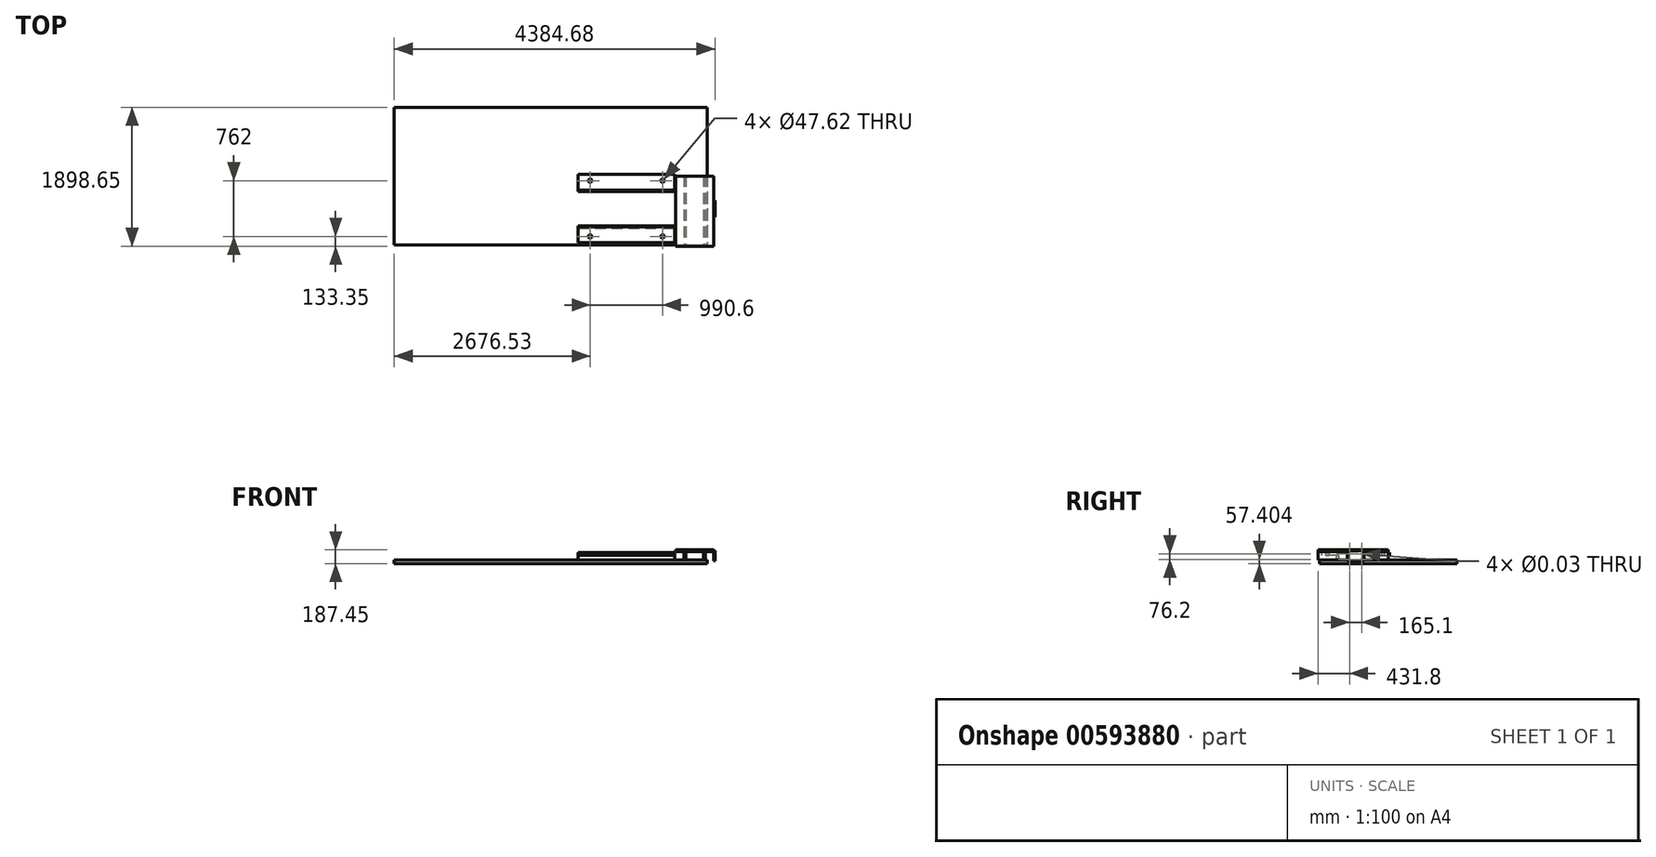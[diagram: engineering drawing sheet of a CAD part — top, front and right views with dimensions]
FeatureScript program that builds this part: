
annotation { "Feature Type Name" : "Feature", "Feature Type Description" : "" }
export const myFeature = defineFeature(function(context is Context, id is Id, definition is map)
    precondition{}
    {
        {
            var Q0;
            Q0=qCreatedBy(makeId("Top.planeOp"),FACE);
            var sketch = newSketch(context, id + "F0", { "sketchPlane" : qUnion([Q0])});
            skLineSegment(sketch, "E0.bottom", {"start": v(-2139.95, 939.8) * mm, "end": v(2139.95, 939.8) * mm});
            skLineSegment(sketch, "E0.top", {"start": v(-2139.95, -939.8) * mm, "end": v(2139.95, -939.8) * mm});
            skLineSegment(sketch, "E0.left", {"start": v(-2139.95, 939.8) * mm, "end": v(-2139.95, -939.8) * mm});
            skLineSegment(sketch, "E0.right", {"start": v(2139.95, 939.8) * mm, "end": v(2139.95, -939.8) * mm});
            skPoint(sketch, "E0.middle", {"position": v(0, 0) * mm});
            skSolve(sketch);
        }
        {
            var Q0;
            Q0 = qSketchRegion(id + "F0", true);
            extrude(context, id + "F1", {"entities" : qUnion([Q0]), "oppositeDirection" : true, "depth" : 50.8 * mm, "offsetDistance" : 25.4 * mm});
        }
        {
            var Q0;
            Q0=makeQuery(id+"F1.opExtrude","CAP_FACE",FACE,{"disambiguationData":[OSD([sQuery(id+"F0.wireOp",EDGE,"E0.bottom"),sQuery(id+"F0.wireOp",EDGE,"E0.top"),sQuery(id+"F0.wireOp",EDGE,"E0.left"),sQuery(id+"F0.wireOp",EDGE,"E0.right")])],"isStart":true});
            var sketch = newSketch(context, id + "F2", { "sketchPlane" : qUnion([Q0])});
            skLineSegment(sketch, "E1.0", {"start": v(1031.87, 939.8) * mm, "end": v(1031.87, -939.8) * mm, "construction": true});
            skLineSegment(sketch, "E2", {"start": v(-2139.95, 0) * mm, "end": v(2139.95, 0) * mm, "construction": true});
            skLineSegment(sketch, "E3.0", {"start": v(-2139.95, -444.5) * mm, "end": v(2139.95, -444.5) * mm, "construction": true});
            skLineSegment(sketch, "E4.0", {"start": v(-2139.95, -679.45) * mm, "end": v(2139.95, -679.45) * mm, "construction": true});
            skLineSegment(sketch, "E5.0", {"start": v(371.47, 939.8) * mm, "end": v(371.47, -939.8) * mm, "construction": true});
            skLineSegment(sketch, "E6.bottom", {"start": v(371.47, -679.45) * mm, "end": v(1692.27, -679.45) * mm});
            skLineSegment(sketch, "E6.top", {"start": v(371.47, -711.2) * mm, "end": v(1692.27, -711.2) * mm});
            skLineSegment(sketch, "E6.left", {"start": v(371.47, -679.45) * mm, "end": v(371.47, -711.2) * mm});
            skLineSegment(sketch, "E6.right", {"start": v(1692.27, -679.45) * mm, "end": v(1692.27, -711.2) * mm});
            skLineSegment(sketch, "E7.MirrorCS", {"start": v(371.47, -209.55) * mm, "end": v(371.47, -177.8) * mm});
            skLineSegment(sketch, "E8.MirrorCS", {"start": v(1692.27, -209.55) * mm, "end": v(1692.27, -177.8) * mm});
            skLineSegment(sketch, "E9.MirrorCS", {"start": v(371.47, -177.8) * mm, "end": v(1692.27, -177.8) * mm});
            skLineSegment(sketch, "E10.MirrorCS", {"start": v(371.47, -209.55) * mm, "end": v(1692.27, -209.55) * mm});
            skSolve(sketch);
        }
        {
            var Q0;
            Q0 = qSketchRegion(id + "F2", true);
            extrude(context, id + "F3", {"entities" : qUnion([Q0]), "operationType" : NewBodyOperationType.ADD, "depth" : 63.5 * mm, "offsetDistance" : 25.4 * mm});
        }
        {
            var Q0;
            Q0=makeQuery(id+"F3.opExtrude","CAP_FACE",FACE,{"disambiguationData":[OSD([sQuery(id+"F2.wireOp",EDGE,"E6.bottom"),sQuery(id+"F2.wireOp",EDGE,"E6.top"),sQuery(id+"F2.wireOp",EDGE,"E6.left"),sQuery(id+"F2.wireOp",EDGE,"E6.right")])],"isStart":false});
            var sketch = newSketch(context, id + "F4", { "sketchPlane" : qUnion([Q0])});
            skLineSegment(sketch, "E11.0", {"start": v(-2139.95, -444.5) * mm, "end": v(2139.95, -444.5) * mm, "construction": true});
            skLineSegment(sketch, "E12.0", {"start": v(-2139.95, -695.45) * mm, "end": v(2139.95, -695.45) * mm, "construction": true});
            skLineSegment(sketch, "E13.0", {"start": v(371.47, 939.8) * mm, "end": v(371.47, -939.8) * mm, "construction": true});
            skLineSegment(sketch, "E14.bottom", {"start": v(371.47, -695.45) * mm, "end": v(1692.27, -695.45) * mm});
            skLineSegment(sketch, "E14.top", {"start": v(371.47, -911.35) * mm, "end": v(1692.27, -911.35) * mm});
            skLineSegment(sketch, "E14.left", {"start": v(371.47, -695.45) * mm, "end": v(371.47, -911.35) * mm});
            skLineSegment(sketch, "E14.right", {"start": v(1692.27, -695.45) * mm, "end": v(1692.27, -911.35) * mm});
            skLineSegment(sketch, "E15.MirrorCS", {"start": v(1692.27, -193.55) * mm, "end": v(1692.27, 22.35) * mm});
            skLineSegment(sketch, "E16.MirrorCS", {"start": v(371.47, -193.55) * mm, "end": v(371.47, 22.35) * mm});
            skLineSegment(sketch, "E17.MirrorCS", {"start": v(371.47, 22.35) * mm, "end": v(1692.27, 22.35) * mm});
            skLineSegment(sketch, "E18.MirrorCS", {"start": v(371.47, -193.55) * mm, "end": v(1692.27, -193.55) * mm});
            skSolve(sketch);
        }
        {
            var Q0;
            Q0 = qSketchRegion(id + "F4", true);
            extrude(context, id + "F5", {"entities" : qUnion([Q0]), "operationType" : NewBodyOperationType.ADD, "depth" : 38.1 * mm, "offsetDistance" : 25.4 * mm});
        }
        {
            var Q0;
            Q0=makeQuery(id+"F5.opExtrude","CAP_FACE",FACE,{"disambiguationData":[OSD([sQuery(id+"F4.wireOp",EDGE,"E14.bottom"),sQuery(id+"F4.wireOp",EDGE,"E14.top"),sQuery(id+"F4.wireOp",EDGE,"E14.left"),sQuery(id+"F4.wireOp",EDGE,"E14.right")])],"isStart":false});
            var sketch = newSketch(context, id + "F6", { "sketchPlane" : qUnion([Q0])});
            skLineSegment(sketch, "E19.0", {"start": v(-2139.95, -444.5) * mm, "end": v(2139.95, -444.5) * mm, "construction": true});
            skLineSegment(sketch, "E20.0", {"start": v(1031.87, 939.8) * mm, "end": v(1031.87, -939.8) * mm, "construction": true});
            skLineSegment(sketch, "E21.0", {"start": v(-2139.95, -825.5) * mm, "end": v(2139.95, -825.5) * mm, "construction": true});
            skLineSegment(sketch, "E22.0", {"start": v(536.57, 939.8) * mm, "end": v(536.57, -939.8) * mm, "construction": true});
            skPoint(sketch, "E23", {"position": v(536.57, -825.5) * mm});
            skPoint(sketch, "E24.0.1.0", {"position": v(536.57, -63.5) * mm});
            skPoint(sketch, "E24.1.0.0", {"position": v(1527.17, -825.5) * mm});
            skPoint(sketch, "E24.1.1.0", {"position": v(1527.17, -63.5) * mm});
            skLineSegment(sketch, "E24.direction1", {"start": v(536.57, -825.5) * mm, "end": v(1527.17, -825.5) * mm, "construction": true});
            skLineSegment(sketch, "E24.direction2", {"start": v(536.57, -825.5) * mm, "end": v(536.57, -63.5) * mm, "construction": true});
            skSolve(sketch);
        }
        {
            var Q0;
            Q0=sQuery(id+"F6.wireOp",VERTEX,"E24.0.1.0");
            var Q1;
            Q1=sQuery(id+"F6.wireOp",VERTEX,"E24.1.1.0");
            var Q2;
            Q2=sQuery(id+"F6.wireOp",VERTEX,"E23");
            var Q3;
            Q3=sQuery(id+"F6.wireOp",VERTEX,"E24.1.0.0");
            var Q4;
            Q4=makeQuery(id+"F1.opExtrude","SWEPT_BODY",BODY,{"disambiguationData":[OSD([sQuery(id+"F0.wireOp",EDGE,"E0.bottom"),sQuery(id+"F0.wireOp",EDGE,"E0.top"),sQuery(id+"F0.wireOp",EDGE,"E0.left"),sQuery(id+"F0.wireOp",EDGE,"E0.right")])]});
            hole(context, id + "F7", {"style" : HoleStyle.SIMPLE, "endStyle" : HoleEndStyle.BLIND, "holeDiameter" : 47.62 * mm, "majorDiameter" : 6.35 * mm, "holeDepth" : 50.8 * mm, "isTappedThrough" : true, "tappedDepth" : 25.4 * mm, "tapClearance" : 3, "locations" : qUnion([Q0, Q1, Q2, Q3]), "scope" : qUnion([Q4])});
        }
        {
            var Q0;
            Q0=makeQuery(id+"F1.opExtrude","CAP_FACE",FACE,{"disambiguationData":[OSD([sQuery(id+"F0.wireOp",EDGE,"E0.bottom"),sQuery(id+"F0.wireOp",EDGE,"E0.top"),sQuery(id+"F0.wireOp",EDGE,"E0.left"),sQuery(id+"F0.wireOp",EDGE,"E0.right")])],"isStart":true});
            var sketch = newSketch(context, id + "F8", { "sketchPlane" : qUnion([Q0])});
            skLineSegment(sketch, "E25.0", {"start": v(-2139.95, -444.5) * mm, "end": v(2139.95, -444.5) * mm, "construction": true});
            skLineSegment(sketch, "E26.0", {"start": v(1031.87, 939.8) * mm, "end": v(1031.87, -939.8) * mm, "construction": true});
            skLineSegment(sketch, "E27.0", {"start": v(1965.33, 939.8) * mm, "end": v(1965.32, -939.8) * mm, "construction": true});
            skLineSegment(sketch, "E28.0", {"start": v(1844.67, 0) * mm, "end": v(1844.67, -958.85) * mm});
            skLineSegment(sketch, "E29.0", {"start": v(1819.27, 0) * mm, "end": v(1819.27, -958.85) * mm});
            skLineSegment(sketch, "E30.0", {"start": v(1819.27, -958.85) * mm, "end": v(1844.67, -958.85) * mm});
            skLineSegment(sketch, "E31.0", {"start": v(-2139.95, 0) * mm, "end": v(1031.87, 0) * mm});
            skLineSegment(sketch, "E32.trimOffspring", {"start": v(1819.27, 0) * mm, "end": v(1844.67, 0) * mm});
            skLineSegment(sketch, "E33.MirrorCS", {"start": v(2111.37, -958.85) * mm, "end": v(2085.97, -958.85) * mm});
            skLineSegment(sketch, "E34.MirrorCS", {"start": v(2111.37, 0) * mm, "end": v(2085.97, 0) * mm});
            skLineSegment(sketch, "E35.MirrorCS", {"start": v(2085.97, 0) * mm, "end": v(2085.97, -958.85) * mm});
            skLineSegment(sketch, "E36.MirrorCS", {"start": v(2111.37, 0) * mm, "end": v(2111.37, -958.85) * mm});
            skSolve(sketch);
        }
        {
            var Q0;
            Q0 = qSketchRegion(id + "F8", true);
            extrude(context, id + "F9", {"entities" : qUnion([Q0]), "operationType" : NewBodyOperationType.ADD, "depth" : 111.25 * mm, "offsetDistance" : 25.4 * mm});
        }
        {
            var Q0;
            Q0=makeQuery(id+"F9.opExtrude","CAP_FACE",FACE,{"disambiguationData":[OSD([sQuery(id+"F8.wireOp",EDGE,"E28.0"),sQuery(id+"F8.wireOp",EDGE,"E29.0"),sQuery(id+"F8.wireOp",EDGE,"E30.0"),sQuery(id+"F8.wireOp",EDGE,"E32.trimOffspring")])],"isStart":false});
            var sketch = newSketch(context, id + "F10", { "sketchPlane" : qUnion([Q0])});
            skLineSegment(sketch, "E37.0", {"start": v(1965.33, 939.8) * mm, "end": v(1965.32, -939.8) * mm, "construction": true});
            skLineSegment(sketch, "E38.0", {"start": v(-2139.95, -444.5) * mm, "end": v(2139.95, -444.5) * mm, "construction": true});
            skLineSegment(sketch, "E39.bottom", {"start": v(1704.97, -958.85) * mm, "end": v(2225.67, -958.85) * mm});
            skLineSegment(sketch, "E39.top", {"start": v(1704.97, 0) * mm, "end": v(2225.67, 0) * mm});
            skLineSegment(sketch, "E39.left", {"start": v(1704.97, -958.85) * mm, "end": v(1704.97, 0) * mm});
            skLineSegment(sketch, "E39.right", {"start": v(2225.67, -958.85) * mm, "end": v(2225.67, 0) * mm});
            skPoint(sketch, "E39.middle", {"position": v(1965.32, -479.42) * mm});
            skLineSegment(sketch, "E40.0", {"start": v(1031.87, 939.8) * mm, "end": v(1031.87, -939.8) * mm, "construction": true});
            skSolve(sketch);
        }
        {
            var Q0;
            Q0 = qSketchRegion(id + "F10", true);
            extrude(context, id + "F11", {"entities" : qUnion([Q0]), "operationType" : NewBodyOperationType.ADD, "depth" : 25.4 * mm, "offsetDistance" : 25.4 * mm});
        }
        {
            var Q0;
            Q0=makeQuery(id+"F11.opExtrude","SWEPT_FACE",FACE,{"disambiguationData":[OSD([sQuery(id+"F10.wireOp",EDGE,"E39.right")])]});
            var sketch = newSketch(context, id + "F12", { "sketchPlane" : qUnion([Q0])});
            skPoint(sketch, "E41.0", {"position": v(-193.55, 82.55) * mm});
            skPoint(sketch, "E42.0", {"position": v(-695.45, 82.55) * mm});
            skLineSegment(sketch, "E43", {"start": v(-695.45, 82.55) * mm, "end": v(-193.55, 82.55) * mm, "construction": true});
            skLineSegment(sketch, "E44", {"start": v(-444.5, 82.55) * mm, "end": v(-444.5, 269.72) * mm, "construction": true});
            skLineSegment(sketch, "E45.0", {"start": v(-558.8, 127) * mm, "end": v(-330.2, 127) * mm});
            skLineSegment(sketch, "E46.0", {"start": v(-558.8, -12.7) * mm, "end": v(-330.2, -12.7) * mm});
            skLineSegment(sketch, "E47.0", {"start": v(-330.2, -12.7) * mm, "end": v(-330.2, 127) * mm});
            skLineSegment(sketch, "E48.MirrorCS", {"start": v(-558.8, -12.7) * mm, "end": v(-558.8, 127) * mm});
            skSolve(sketch);
        }
        {
            var Q0;
            Q0 = qSketchRegion(id + "F12", true);
            extrude(context, id + "F13", {"entities" : qUnion([Q0]), "operationType" : NewBodyOperationType.ADD, "depth" : 19.05 * mm, "offsetDistance" : 25.4 * mm});
        }
        {
            var Q0;
            Q0=makeQuery(id+"F13.opExtrude","CAP_FACE",FACE,{"disambiguationData":[OSD([sQuery(id+"F12.wireOp",EDGE,"E45.0"),sQuery(id+"F12.wireOp",EDGE,"E46.0"),sQuery(id+"F12.wireOp",EDGE,"E47.0"),sQuery(id+"F12.wireOp",EDGE,"E48.MirrorCS")])],"isStart":false});
            var sketch = newSketch(context, id + "F14", { "sketchPlane" : qUnion([Q0])});
            skLineSegment(sketch, "E49.0", {"start": v(-958.85, 82.8) * mm, "end": v(0, 82.8) * mm, "construction": true});
            skLineSegment(sketch, "E50.0", {"start": v(-958.85, 6.6) * mm, "end": v(0, 6.6) * mm, "construction": true});
            skLineSegment(sketch, "E51", {"start": v(-444.5, -12.7) * mm, "end": v(-444.5, 245.05) * mm, "construction": true});
            skLineSegment(sketch, "E52.0", {"start": v(-361.95, -12.7) * mm, "end": v(-361.95, 245.05) * mm, "construction": true});
            skLineSegment(sketch, "E53.MirrorCS", {"start": v(-527.05, -12.7) * mm, "end": v(-527.05, 245.05) * mm, "construction": true});
            skPoint(sketch, "E54", {"position": v(-527.05, 6.6) * mm});
            skPoint(sketch, "E55", {"position": v(-527.05, 82.8) * mm});
            skPoint(sketch, "E56", {"position": v(-361.95, 82.8) * mm});
            skPoint(sketch, "E57", {"position": v(-361.95, 6.6) * mm});
            skSolve(sketch);
        }
        {
            var Q0;
            Q0=sQuery(id+"F14.wireOp",VERTEX,"E55");
            var Q1;
            Q1=sQuery(id+"F14.wireOp",VERTEX,"E54");
            var Q2;
            Q2=sQuery(id+"F14.wireOp",VERTEX,"E57");
            var Q3;
            Q3=sQuery(id+"F14.wireOp",VERTEX,"E56");
            var Q4;
            Q4=makeQuery(id+"F1.opExtrude","SWEPT_BODY",BODY,{"disambiguationData":[OSD([sQuery(id+"F0.wireOp",EDGE,"E0.bottom"),sQuery(id+"F0.wireOp",EDGE,"E0.top"),sQuery(id+"F0.wireOp",EDGE,"E0.left"),sQuery(id+"F0.wireOp",EDGE,"E0.right")])]});
            hole(context, id + "F15", {"style" : HoleStyle.SIMPLE, "endStyle" : HoleEndStyle.BLIND, "standardTappedOrClearance" : lookupTablePath({ "standard" : "ANSI", "size" : "11/16 (0.69)", "type" : "Drilled" }), "standardBlindInLast" : lookupTablePath({ "standard" : "ANSI", "size" : "11/16", "type" : "Drilled" }), "holeDiameter" : 11 / 406.4 * mm, "majorDiameter" : 6.35 * mm, "holeDepth" : 50.8 * mm, "isTappedThrough" : true, "tappedDepth" : 25.4 * mm, "tapClearance" : 3, "locations" : qUnion([Q0, Q1, Q2, Q3]), "scope" : qUnion([Q4])});
        }
    });
